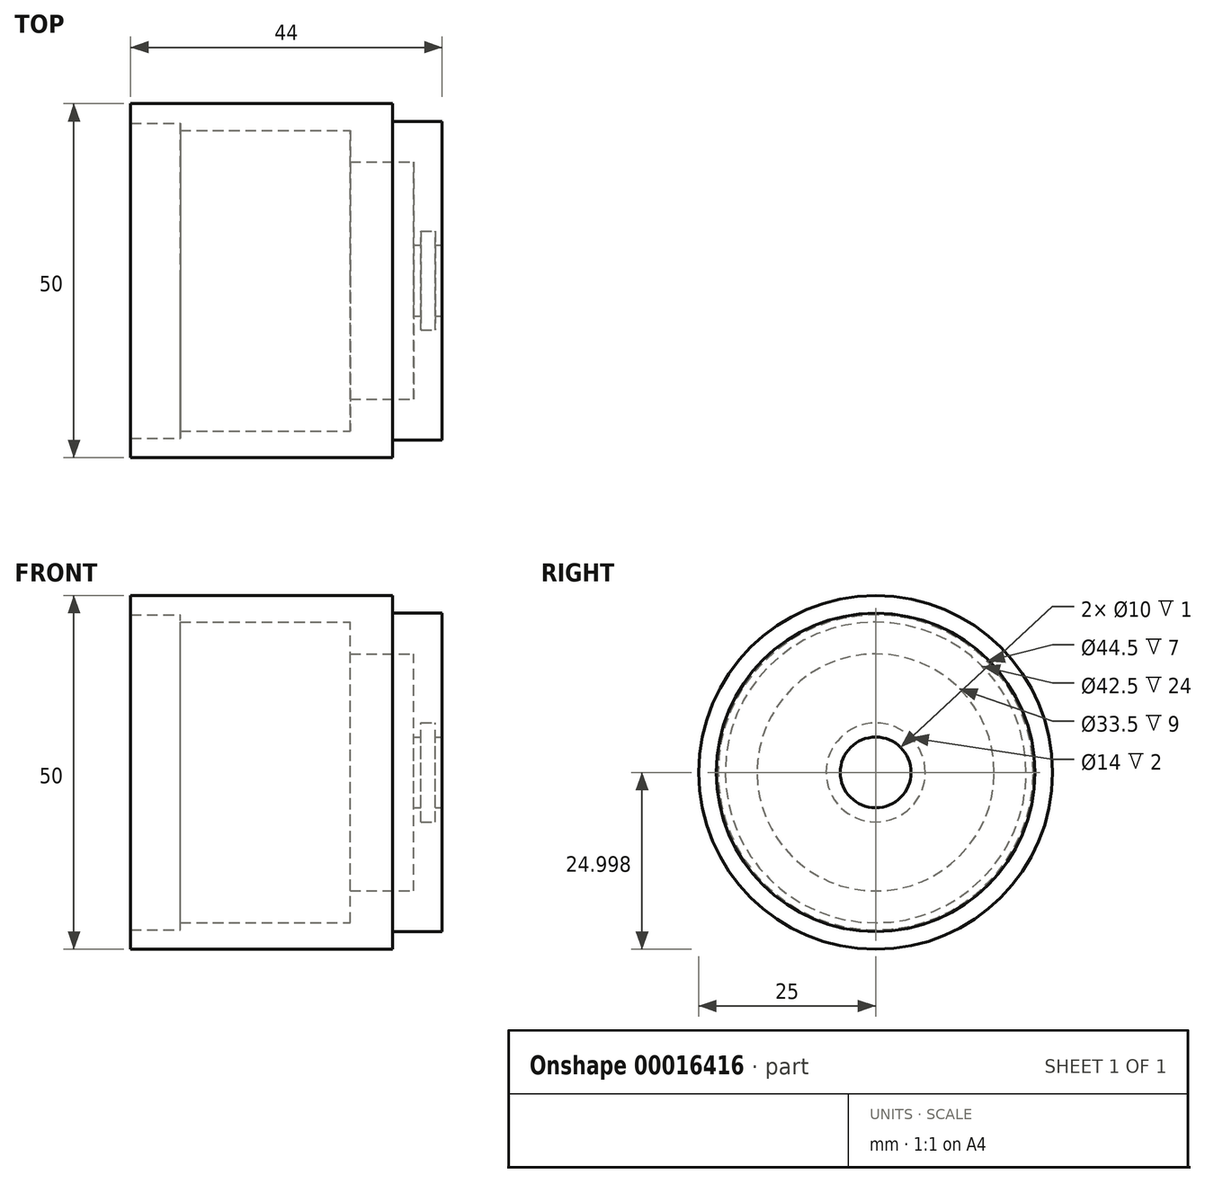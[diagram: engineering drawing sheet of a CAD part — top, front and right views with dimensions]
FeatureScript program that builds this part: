
annotation { "Feature Type Name" : "Feature", "Feature Type Description" : "" }
export const myFeature = defineFeature(function(context is Context, id is Id, definition is map)
    precondition{}
    {
        {
            var Q0;
            Q0=qCreatedBy(makeId("Front.planeOp"),FACE);
            var sketch = newSketch(context, id + "F0", { "sketchPlane" : qUnion([Q0])});
            skLineSegment(sketch, "E0", {"start": v(-5.43, 1.3) * mm, "end": v(-5.43, 18.8) * mm});
            skLineSegment(sketch, "E1", {"start": v(-5.43, 18.8) * mm, "end": v(-12.43, 18.8) * mm});
            skLineSegment(sketch, "E2", {"start": v(-12.43, 18.8) * mm, "end": v(-12.43, 21.3) * mm});
            skLineSegment(sketch, "E3", {"start": v(-12.43, 21.3) * mm, "end": v(-49.43, 21.3) * mm});
            skLineSegment(sketch, "E4", {"start": v(-49.43, 21.3) * mm, "end": v(-49.43, 18.55) * mm});
            skLineSegment(sketch, "E5", {"start": v(-9.43, 13.05) * mm, "end": v(-9.43, 1.3) * mm});
            skLineSegment(sketch, "E6", {"start": v(-6.43, 1.3) * mm, "end": v(-5.43, 1.3) * mm});
            skLineSegment(sketch, "E7.0", {"start": v(-8.43, 3.3) * mm, "end": v(-8.43, 1.3) * mm});
            skLineSegment(sketch, "E8.0", {"start": v(-6.43, 3.3) * mm, "end": v(-6.43, 1.3) * mm});
            skLineSegment(sketch, "E9", {"start": v(-5.43, 1.3) * mm, "end": v(-6.43, 1.3) * mm});
            skLineSegment(sketch, "E10.0", {"start": v(-17.43, -3.7) * mm, "end": v(-43.89, -3.7) * mm, "construction": true});
            skLineSegment(sketch, "E11.trimOffspring", {"start": v(-42.43, 17.55) * mm, "end": v(-18.43, 17.55) * mm});
            skLineSegment(sketch, "E12.0", {"start": v(-49.43, 18.55) * mm, "end": v(-42.43, 18.55) * mm});
            skLineSegment(sketch, "E13.0", {"start": v(-42.43, 18.55) * mm, "end": v(-42.43, 17.55) * mm});
            skLineSegment(sketch, "E14.0", {"start": v(-18.43, 17.55) * mm, "end": v(-18.43, 13.05) * mm});
            skLineSegment(sketch, "E15.0", {"start": v(-18.43, 13.05) * mm, "end": v(-9.43, 13.05) * mm});
            skPoint(sketch, "E16.orphan", {"position": v(-9.43, 1.3) * mm});
            skLineSegment(sketch, "E17.trimOffspring", {"start": v(-19.43, 1.3) * mm, "end": v(-43.89, 1.3) * mm, "construction": true});
            skLineSegment(sketch, "E18.trimOffspring", {"start": v(-8.43, 1.3) * mm, "end": v(-9.43, 1.3) * mm});
            skLineSegment(sketch, "E19", {"start": v(-8.43, 3.3) * mm, "end": v(-6.43, 3.3) * mm});
            skSolve(sketch);
        }
        {
            var Q0;
            Q0=makeQuery(id+"F0.imprint","IMPRINT",FACE,{"disambiguationData":[TD([[makeQuery(id+"F0.imprint","IMPRINT",EDGE,{"derivedFrom":sQuery(id+"F0.wireOp",EDGE,"E0")}),1.0]])]});
            var Q1;
            Q1=sQuery(id+"F0.wireOp",EDGE,"E10.0");
            revolve(context, id + "F1", {"entities" : qUnion([Q0]), "axis" : qUnion([Q1]), "revolveType" : RevolveType.FULL});
        }
    });
